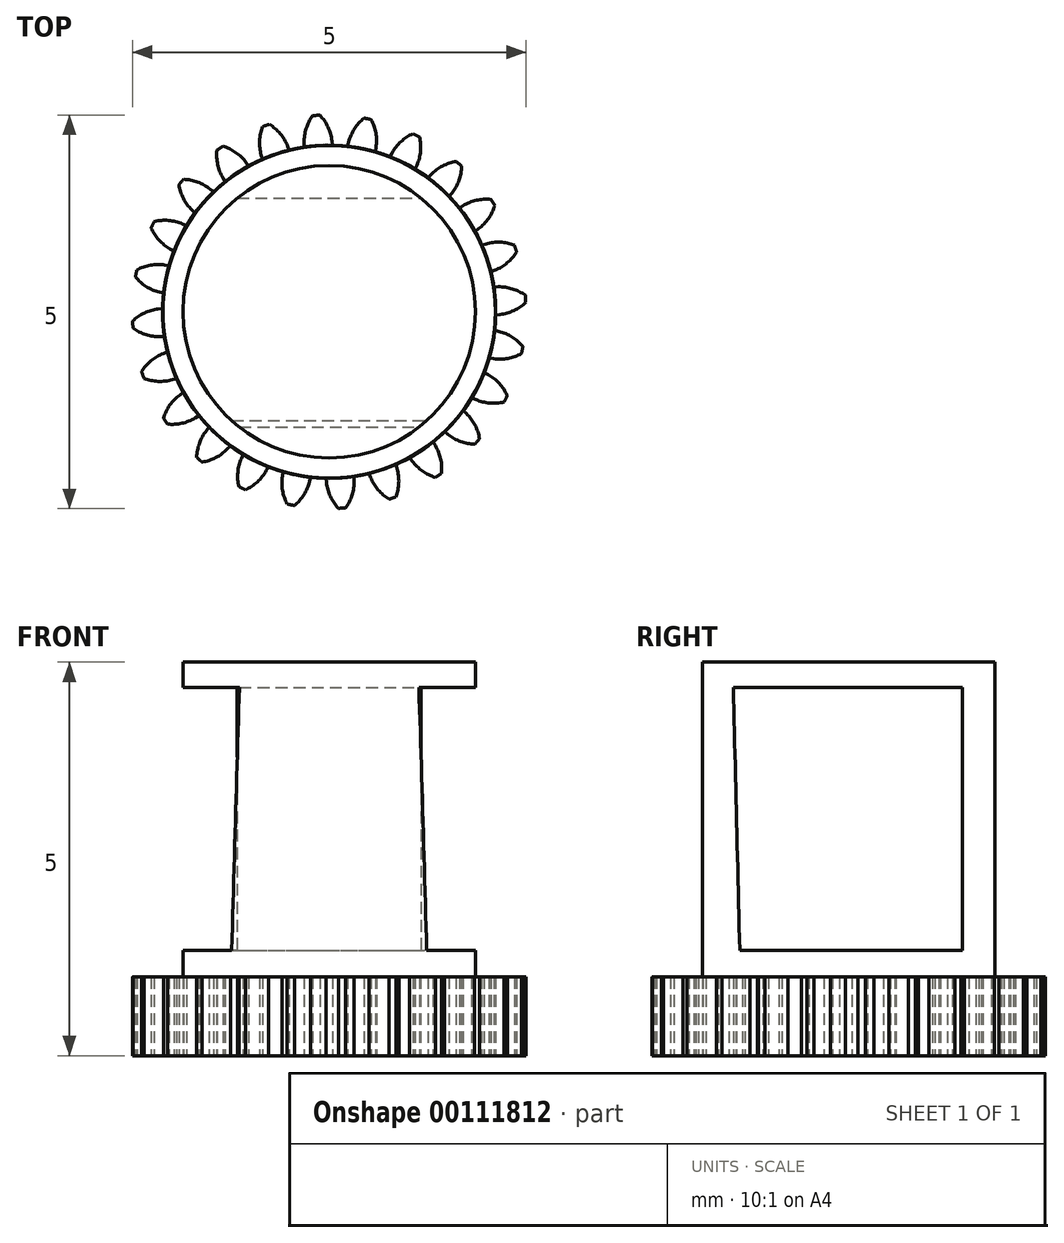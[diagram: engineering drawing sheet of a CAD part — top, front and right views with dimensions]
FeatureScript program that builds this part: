
annotation { "Feature Type Name" : "Feature", "Feature Type Description" : "" }
export const myFeature = defineFeature(function(context is Context, id is Id, definition is map)
    precondition{}
    {
        {
            var Q0;
            Q0=qCreatedBy(makeId("Top.planeOp"),FACE);
            var sketch = newSketch(context, id + "F0", { "sketchPlane" : qUnion([Q0])});
            skCircle(sketch, "E0", {"center": v(0, 0) * mm, "radius": 2.12 * mm});
            skCircle(sketch, "E1", {"center": v(0, 0) * mm, "radius": 2.31 * mm, "construction": true});
            skCircle(sketch, "E2", {"center": v(0, 0) * mm, "radius": 2.5 * mm, "construction": true});
            skLineSegment(sketch, "E3", {"start": v(0, 0) * mm, "end": v(0, 5.05) * mm, "construction": true});
            skLineSegment(sketch, "E4", {"start": v(0, 0) * mm, "end": v(-0.34, 5.17) * mm, "construction": true});
            skLineSegment(sketch, "E5", {"start": v(0, 2.31) * mm, "end": v(-5.24, 2.31) * mm, "construction": true});
            skLineSegment(sketch, "E6", {"start": v(0, 2.31) * mm, "end": v(-5.49, 0.31) * mm, "construction": true});
            skCircle(sketch, "E7", {"center": v(0, 2.31) * mm, "radius": 0.57 * mm, "construction": true});
            skCircle(sketch, "E8", {"center": v(0, 0) * mm, "radius": 2.17 * mm, "construction": true});
            skCircle(sketch, "E9", {"center": v(-0.54, 2.1) * mm, "radius": 0.57 * mm, "construction": true});
            skArc(sketch, "E10", {"start": v(-0.12, 2.5) * mm, "mid": v(-0.27, 2.61) * mm, "end": v(-0.45, 2.67) * mm});
            skArc(sketch, "E11", {"start": v(0.03, 2.17) * mm, "mid": v(-0.02, 2.35) * mm, "end": v(-0.12, 2.5) * mm});
            skArc(sketch, "E12.MirrorCS", {"start": v(-0.32, 2.15) * mm, "mid": v(-0.3, 2.33) * mm, "end": v(-0.2, 2.5) * mm});
            skLineSegment(sketch, "E13", {"start": v(-0.32, 2.15) * mm, "end": v(-0.32, 2.1) * mm});
            skLineSegment(sketch, "E14", {"start": v(0.03, 2.17) * mm, "end": v(0.04, 2.11) * mm});
            skArc(sketch, "E15", {"start": v(-0.12, 2.5) * mm, "mid": v(-0.16, 2.5) * mm, "end": v(-0.2, 2.5) * mm});
            skSolve(sketch);
        }
        {
            var Q0;
            {var subQ0=sQuery(id+"F0.wireOp",EDGE,"E0");var subQ1=makeQuery(id+"F0.imprint","INTERSECT",VERTEX,{"derivedFrom":[subQ0,sQuery(id+"F0.wireOp",EDGE,"E13")]});Q0=makeQuery(id+"F0.imprint","IMPRINT",FACE,{"disambiguationData":[TD([[makeQuery(id+"F0.imprint","IMPRINT",EDGE,{"disambiguationData":[TD([[subQ1,1.0]])],"derivedFrom":subQ0}),1.0]])]});}
            var Q1;
            Q1=makeQuery(id+"F0.imprint","IMPRINT",FACE,{"disambiguationData":[TD([[makeQuery(id+"F0.imprint","IMPRINT",EDGE,{"derivedFrom":sQuery(id+"F0.wireOp",EDGE,"E11")}),1.0]])]});
            extrude(context, id + "F1", {"entities" : qUnion([Q0, Q1]), "depth" : 1 * mm});
        }
        {
            var Q0;
            Q0=makeQuery(id+"F1.opExtrude","SWEPT_BODY",BODY,{"disambiguationData":[OSD([sQuery(id+"F0.wireOp",EDGE,"E0"),sQuery(id+"F0.wireOp",EDGE,"E11"),sQuery(id+"F0.wireOp",EDGE,"E12.MirrorCS"),sQuery(id+"F0.wireOp",EDGE,"E13"),sQuery(id+"F0.wireOp",EDGE,"E14"),sQuery(id+"F0.wireOp",EDGE,"E15")])]});
            var Q1;
            Q1=makeQuery(id+"F1.opExtrude","SWEPT_FACE",FACE,{"disambiguationData":[OSD([sQuery(id+"F0.wireOp",EDGE,"E0")])]});
            circularPattern(context, id + "F2", {"entities" : qUnion([Q0]), "axis" : qUnion([Q1]), "angle" : 15 * degree, "instanceCount" : 24});
        }
        {
            var Q0;
            Q0=qCreatedBy(makeId("Top.planeOp"),FACE);
            var sketch = newSketch(context, id + "F3", { "sketchPlane" : qUnion([Q0])});
            skCircle(sketch, "E16", {"center": v(0, 0) * mm, "radius": 1.86 * mm});
            skSolve(sketch);
        }
        {
            var Q0;
            Q0 = qSketchRegion(id + "F3", true);
            extrude(context, id + "F4", {"entities" : qUnion([Q0]), "depth" : 5 * mm});
        }
        {
            var Q0;
            Q0=qCreatedBy(makeId("Right.planeOp"),FACE);
            var sketch = newSketch(context, id + "F5", { "sketchPlane" : qUnion([Q0])});
            skLineSegment(sketch, "E17", {"start": v(-1.47, 4.68) * mm, "end": v(1.44, 4.68) * mm});
            skLineSegment(sketch, "E18", {"start": v(1.44, 4.68) * mm, "end": v(1.44, 1.34) * mm});
            skLineSegment(sketch, "E19", {"start": v(1.44, 1.34) * mm, "end": v(-1.38, 1.34) * mm});
            skLineSegment(sketch, "E20", {"start": v(-1.38, 1.34) * mm, "end": v(-1.47, 4.68) * mm});
            skSolve(sketch);
        }
        {
            var Q0;
            Q0 = qSketchRegion(id + "F5", true);
            extrude(context, id + "F6", {"entities" : qUnion([Q0]), "operationType" : NewBodyOperationType.REMOVE, "endBound" : BoundingType.SYMMETRIC, "oppositeDirection" : true, "depth" : 25 * mm});
        }
    });
